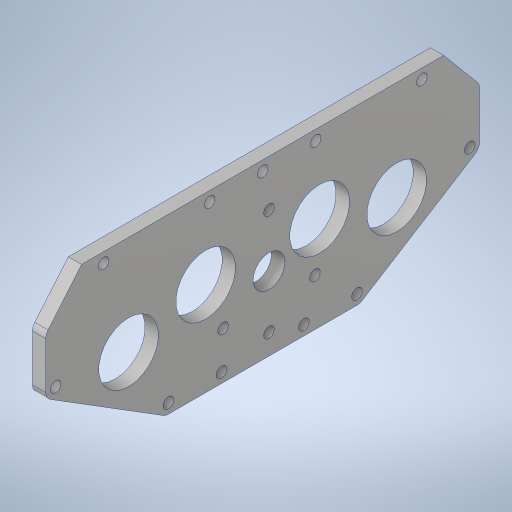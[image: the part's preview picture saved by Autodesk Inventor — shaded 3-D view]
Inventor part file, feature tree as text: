
AUTODESK INVENTOR PART (.ipt)
format: ipt  version: 2023.4 (Build 274418000, 418)  size: 375,296 bytes
history: native  units: in
note: dims shown in document units (in); Inventor stores cm internally (conversion verified against a paired STEP export)
features: sketch x2, hole x2, extrude x1, mirror x1
ambient origin geometry x8: Origin, YZ Plane, XZ Plane, XY Plane, X Axis, Y Axis, Z Axis, Center Point
bodies: Solid1 (feature_tree)
feature tree (6):
  sketch  "Sketch1"  dims[d0=0.125in d1=28.0in]
  sketch  "Sketch3"  dims[d2=2.0in d3=1.0in d4=5.5in d5=3.0in d6=1.0in d7=32.0in d8=1.0in d9=0.375in d10=14.0in d11=0.812in d12=0.438in d13=0.3in d23=2.63in d24=2.0in d30=2.256in d31=0.5in d32=2.0in d33=1.0in d34=2.0in d35=0.5in d36=2.0in d37=2.4in d38=1.5in d39=1.375in d40=0.375in d41=1.125in d42=1.125in d43=2.3622in d45=360.0deg d47=2.0in d48=1.0in d49=0.875in d50=0.3in d51=1.0in d52=0.75in d55=0.8933in d57=0.25in d58=0.0in d59=0.201in d60=0.75in d61=0.385in d62=0.25in d63=0.5635in d64=1.0in d65=0.8108in d66=0.6in d68=1.125in d69=1.5in d70=0.201in d71=0.75in d72=0.375in d73=0.25in d74=0.5635in d75=1.0in d76=0.8108in]
  extrude  "Extrusion1"  Depth=28.0in
  hole  "Mount Holes"  [1 undecoded]
  hole  "Motor Mount"  [1 undecoded]
  mirror  "Mirror1"
note: 2 required parameter values undecoded (feature->parameter linkage not recoverable at this tier; creation-order binding heuristic only, values carry confidence <= 0.55)
